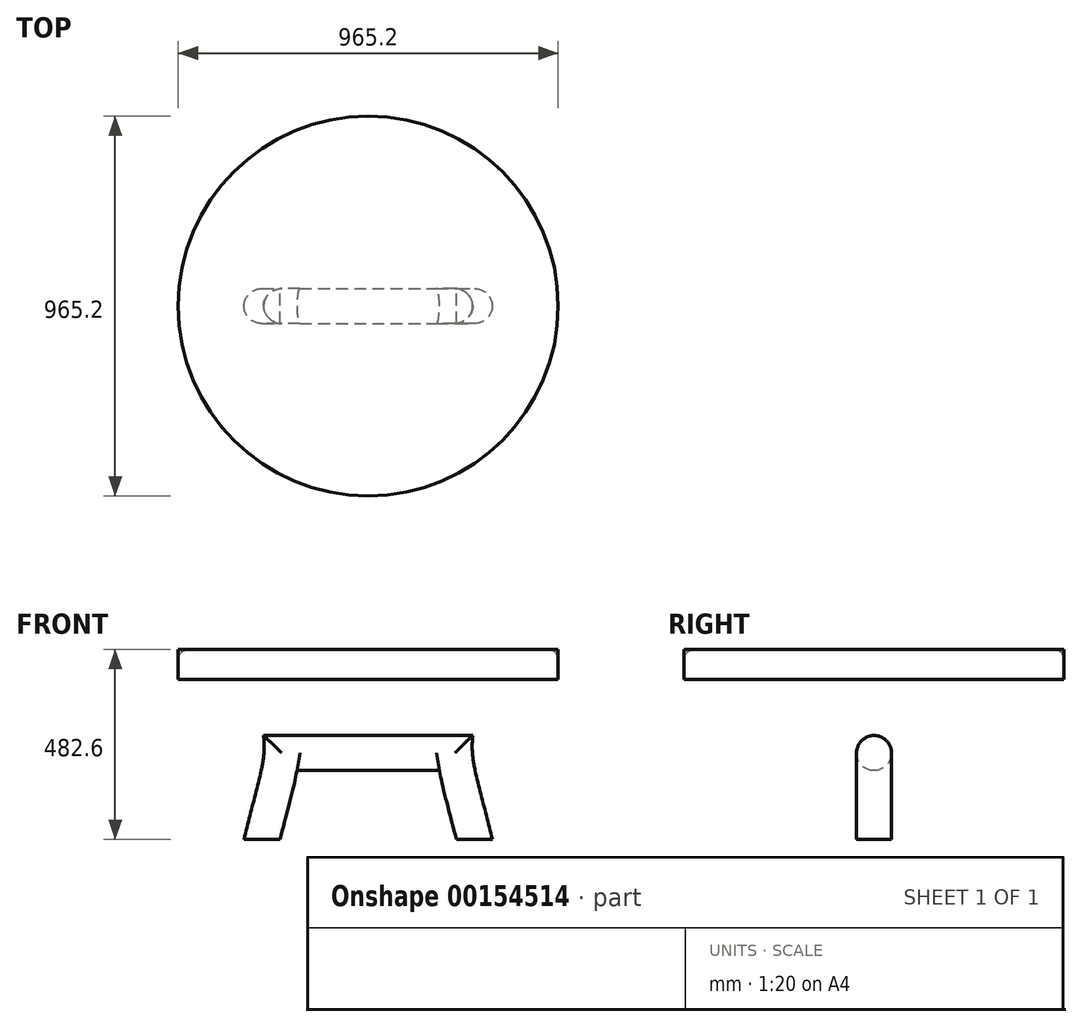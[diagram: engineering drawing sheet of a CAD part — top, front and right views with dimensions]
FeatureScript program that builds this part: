
annotation { "Feature Type Name" : "Feature", "Feature Type Description" : "" }
export const myFeature = defineFeature(function(context is Context, id is Id, definition is map)
    precondition{}
    {
        {
            var Q0;
            Q0=qCreatedBy(makeId("Top.planeOp"),FACE);
            var sketch = newSketch(context, id + "F0", { "sketchPlane" : qUnion([Q0])});
            skCircle(sketch, "E0", {"center": v(0, 0) * mm, "radius": 482.6 * mm});
            skSolve(sketch);
        }
        {
            var Q0;
            Q0=makeQuery(id+"F0.imprint","IMPRINT",FACE,{"disambiguationData":[TD([[makeQuery(id+"F0.imprint","IMPRINT",EDGE,{"derivedFrom":sQuery(id+"F0.wireOp",EDGE,"E0")}),1.0]])]});
            extrude(context, id + "F1", {"entities" : qUnion([Q0]), "oppositeDirection" : true, "depth" : 76.2 * mm});
        }
        {
            var Q0;
            Q0=qCreatedBy(makeId("Front.planeOp"),FACE);
            var sketch = newSketch(context, id + "F2", { "sketchPlane" : qUnion([Q0])});
            skFitSpline(sketch, "E1", {"points": [v(-350.08, -37.61) * mm, v(-265.93, -218.8) * mm, v(-315.3, -482.6) * mm], "startDerivative": vector(306.3, -378.15) * mm, "endDerivative": vector(-196.23, -818.74) * mm});
            skLineSegment(sketch, "E2", {"start": v(-315.3, -482.6) * mm, "end": v(-223.82, -482.6) * mm});
            skFitSpline(sketch, "E3.0", {"points": [v(-281, 18.35) * mm, v(-273.37, 8.93) * mm, v(-258.87, -10.26) * mm, v(-239.44, -39.86) * mm, v(-222.35, -70.1) * mm, v(-207.68, -100.8) * mm, v(-195.49, -131.86) * mm, v(-187.5, -157.95) * mm, v(-182.5, -178.94) * mm, v(-180, -192.1) * mm, v(-178.36, -202.68) * mm, v(-177, -213.27) * mm, v(-175.82, -226.5) * mm, v(-175.23, -242.3) * mm, v(-175.47, -257.95) * mm, v(-176.47, -273.39) * mm, v(-178.13, -288.6) * mm, v(-180.37, -303.66) * mm, v(-183.1, -318.64) * mm, v(-186.24, -333.69) * mm, v(-190.93, -354.09) * mm, v(-197.62, -380.68) * mm, v(-206.85, -415.9) * mm, v(-217.23, -455.92) * mm, v(-224.87, -486.7) * mm, v(-228.85, -503.32) * mm]});
            skLineSegment(sketch, "E4", {"start": v(0, 0) * mm, "end": v(0, -373.88) * mm, "construction": true});
            skFitSpline(sketch, "E5.MirrorCS", {"points": [v(350.08, -37.61) * mm, v(265.93, -218.8) * mm, v(315.3, -482.6) * mm], "startDerivative": vector(-306.3, -378.15) * mm, "endDerivative": vector(196.23, -818.74) * mm});
            skFitSpline(sketch, "E6.0", {"points": [v(281, 18.35) * mm, v(273.37, 8.93) * mm, v(258.87, -10.26) * mm, v(239.44, -39.86) * mm, v(222.35, -70.1) * mm, v(207.68, -100.8) * mm, v(195.49, -131.86) * mm, v(187.5, -157.95) * mm, v(182.5, -178.94) * mm, v(180, -192.1) * mm, v(178.36, -202.68) * mm, v(177, -213.27) * mm, v(175.82, -226.5) * mm, v(175.23, -242.3) * mm, v(175.47, -257.95) * mm, v(176.47, -273.39) * mm, v(178.13, -288.6) * mm, v(180.37, -303.66) * mm, v(183.1, -318.64) * mm, v(186.24, -333.69) * mm, v(190.93, -354.09) * mm, v(197.62, -380.68) * mm, v(206.85, -415.9) * mm, v(217.23, -455.92) * mm, v(224.87, -486.7) * mm, v(228.85, -503.32) * mm]});
            skLineSegment(sketch, "E7", {"start": v(-350.08, -37.61) * mm, "end": v(-241.28, -37.61) * mm});
            skLineSegment(sketch, "E8", {"start": v(350.08, -37.61) * mm, "end": v(241.28, -37.61) * mm});
            skLineSegment(sketch, "E9", {"start": v(265.93, -218.8) * mm, "end": v(-265.93, -218.8) * mm});
            skLineSegment(sketch, "E10", {"start": v(271.65, -307.7) * mm, "end": v(-271.65, -307.7) * mm});
            skLineSegment(sketch, "E11", {"start": v(223.82, -482.6) * mm, "end": v(315.3, -482.6) * mm});
            skSolve(sketch);
        }
        {
            var Q0;
            {var subQ0=sQuery(id+"F2.wireOp",EDGE,"E7");var subQ1=sQuery(id+"F2.wireOp",EDGE,"E1");var subQ2=makeQuery(id+"F2.imprint","INTERSECT",VERTEX,{"derivedFrom":[subQ1,subQ0]});Q0=makeQuery(id+"F2.imprint","IMPRINT",FACE,{"disambiguationData":[TD([[makeQuery(id+"F2.imprint","IMPRINT",EDGE,{"disambiguationData":[TD([[subQ2,-1.0]])],"derivedFrom":subQ1}),1.0]])]});}
            var Q1;
            {var subQ0=sQuery(id+"F2.wireOp",EDGE,"E9");var subQ1=sQuery(id+"F2.wireOp",EDGE,"E1");var subQ2=makeQuery(id+"F2.imprint","INTERSECT",VERTEX,{"derivedFrom":[subQ1,subQ0]});Q1=makeQuery(id+"F2.imprint","IMPRINT",FACE,{"disambiguationData":[TD([[makeQuery(id+"F2.imprint","IMPRINT",EDGE,{"disambiguationData":[TD([[subQ2,-1.0]])],"derivedFrom":subQ1}),1.0]])]});}
            var Q2;
            {var subQ0=sQuery(id+"F2.wireOp",EDGE,"E10");var subQ1=sQuery(id+"F2.wireOp",EDGE,"E3.0");var subQ2=makeQuery(id+"F2.imprint","INTERSECT",VERTEX,{"derivedFrom":[subQ1,subQ0]});Q2=makeQuery(id+"F2.imprint","IMPRINT",FACE,{"disambiguationData":[TD([[makeQuery(id+"F2.imprint","IMPRINT",EDGE,{"disambiguationData":[TD([[subQ2,1.0]])],"derivedFrom":subQ1}),1.0]])]});}
            var Q3;
            {var subQ0=sQuery(id+"F2.wireOp",EDGE,"E8");var subQ1=sQuery(id+"F2.wireOp",EDGE,"E5.MirrorCS");var subQ2=makeQuery(id+"F2.imprint","INTERSECT",VERTEX,{"derivedFrom":[subQ1,subQ0]});Q3=makeQuery(id+"F2.imprint","IMPRINT",FACE,{"disambiguationData":[TD([[makeQuery(id+"F2.imprint","IMPRINT",EDGE,{"disambiguationData":[TD([[subQ2,-1.0]])],"derivedFrom":subQ1}),-1.0]])]});}
            var Q4;
            {var subQ0=sQuery(id+"F2.wireOp",EDGE,"E9");var subQ1=sQuery(id+"F2.wireOp",EDGE,"E5.MirrorCS");var subQ2=makeQuery(id+"F2.imprint","INTERSECT",VERTEX,{"derivedFrom":[subQ1,subQ0]});Q4=makeQuery(id+"F2.imprint","IMPRINT",FACE,{"disambiguationData":[TD([[makeQuery(id+"F2.imprint","IMPRINT",EDGE,{"disambiguationData":[TD([[subQ2,-1.0]])],"derivedFrom":subQ1}),-1.0]])]});}
            var Q5;
            {var subQ0=sQuery(id+"F2.wireOp",EDGE,"E2");Q5=makeQuery(id+"F2.imprint","IMPRINT",FACE,{"disambiguationData":[TD([[makeQuery(id+"F2.imprint","IMPRINT",EDGE,{"derivedFrom":subQ0}),1.0]])]});}
            var Q6;
            {var subQ0=sQuery(id+"F2.wireOp",EDGE,"E11");var subQ1=sQuery(id+"F2.wireOp",EDGE,"E5.MirrorCS");var subQ2=makeQuery(id+"F2.imprint","INTERSECT",VERTEX,{"derivedFrom":[subQ1,subQ0]});Q6=makeQuery(id+"F2.imprint","IMPRINT",FACE,{"disambiguationData":[TD([[makeQuery(id+"F2.imprint","IMPRINT",EDGE,{"disambiguationData":[TD([[subQ2,1.0]])],"derivedFrom":subQ1}),-1.0]])]});}
            extrude(context, id + "F3", {"entities" : qUnion([Q0, Q1, Q2, Q3, Q4, Q5, Q6]), "operationType" : NewBodyOperationType.ADD, "depth" : 88.9 * mm, "symmetric" : true});
        }
        {
            var Q0;
            Q0=makeQuery(id+"F1.opExtrude","SWEPT_BODY",BODY,{"disambiguationData":[OSD([sQuery(id+"F0.wireOp",EDGE,"E0")])]});
            var Q1;
            Q1=makeQuery(id+"F1.opExtrude","CAP_EDGE",EDGE,{"disambiguationData":[OSD([sQuery(id+"F0.wireOp",EDGE,"E0")])],"isStart":true});
            circularPattern(context, id + "F4", {"operationType" : NewBodyOperationType.ADD, "entities" : qUnion([Q0]), "axis" : qUnion([Q1]), "angle" : 90 * degree, "instanceCount" : 2});
        }
        {
            var Q0;
            Q0=makeQuery(id+"F4.opPattern","COPY",EDGE,{"derivedFrom":makeQuery(id+"F3.opExtrude","CAP_EDGE",EDGE,{"disambiguationData":[OSD([sQuery(id+"F2.wireOp",EDGE,"E1")])],"isStart":false}),"instanceName":"1"});
            var Q1;
            Q1=makeQuery(id+"F4.opPattern","COPY",EDGE,{"derivedFrom":makeQuery(id+"F3.opExtrude","CAP_EDGE",EDGE,{"disambiguationData":[OSD([sQuery(id+"F2.wireOp",EDGE,"E1")])],"isStart":true}),"instanceName":"1"});
            var Q2;
            Q2=makeQuery(id+"F3.opExtrude","CAP_EDGE",EDGE,{"disambiguationData":[OSD([sQuery(id+"F2.wireOp",EDGE,"E5.MirrorCS")])],"isStart":false});
            var Q3;
            Q3=makeQuery(id+"F3.opExtrude","CAP_EDGE",EDGE,{"disambiguationData":[OSD([sQuery(id+"F2.wireOp",EDGE,"E5.MirrorCS")])],"isStart":true});
            var Q4;
            Q4=makeQuery(id+"F3.opExtrude","CAP_EDGE",EDGE,{"disambiguationData":[OSD([sQuery(id+"F2.wireOp",EDGE,"E1")])],"isStart":false});
            var Q5;
            Q5=makeQuery(id+"F3.opExtrude","CAP_EDGE",EDGE,{"disambiguationData":[OSD([sQuery(id+"F2.wireOp",EDGE,"E1")])],"isStart":true});
            var Q6;
            Q6=makeQuery(id+"F4.opPattern","COPY",EDGE,{"derivedFrom":makeQuery(id+"F3.opExtrude","CAP_EDGE",EDGE,{"disambiguationData":[OSD([sQuery(id+"F2.wireOp",EDGE,"E5.MirrorCS")])],"isStart":true}),"instanceName":"1"});
            var Q7;
            Q7=makeQuery(id+"F4.opPattern","COPY",EDGE,{"derivedFrom":makeQuery(id+"F3.opExtrude","CAP_EDGE",EDGE,{"disambiguationData":[OSD([sQuery(id+"F2.wireOp",EDGE,"E5.MirrorCS")])],"isStart":false}),"instanceName":"1"});
            var Q8;
            {var subQ0=makeQuery(id+"F3.opExtrude","CAP_FACE",FACE,{"disambiguationData":[OSD([sQuery(id+"F2.wireOp",EDGE,"E1"),sQuery(id+"F2.wireOp",EDGE,"E2"),sQuery(id+"F2.wireOp",EDGE,"E3.0"),sQuery(id+"F2.wireOp",EDGE,"E5.MirrorCS"),sQuery(id+"F2.wireOp",EDGE,"E6.0"),sQuery(id+"F2.wireOp",EDGE,"E7"),sQuery(id+"F2.wireOp",EDGE,"E8"),sQuery(id+"F2.wireOp",EDGE,"E9"),sQuery(id+"F2.wireOp",EDGE,"E10"),sQuery(id+"F2.wireOp",EDGE,"E11")])],"isStart":false});Q8=makeQuery(id+"F4.boolean.opBoolean","INTERSECT",EDGE,{"derivedFrom":[subQ0,makeQuery(id+"F4.opPattern","COPY",FACE,{"derivedFrom":subQ0,"instanceName":"1"})]});}
            var Q9;
            {var subQ0=sQuery(id+"F2.wireOp",EDGE,"E11");var subQ1=sQuery(id+"F2.wireOp",EDGE,"E10");var subQ2=sQuery(id+"F2.wireOp",EDGE,"E9");var subQ3=sQuery(id+"F2.wireOp",EDGE,"E8");var subQ4=sQuery(id+"F2.wireOp",EDGE,"E7");var subQ5=sQuery(id+"F2.wireOp",EDGE,"E6.0");var subQ6=sQuery(id+"F2.wireOp",EDGE,"E5.MirrorCS");var subQ7=sQuery(id+"F2.wireOp",EDGE,"E3.0");var subQ8=sQuery(id+"F2.wireOp",EDGE,"E2");var subQ9=sQuery(id+"F2.wireOp",EDGE,"E1");Q9=makeQuery(id+"F4.boolean.opBoolean","INTERSECT",EDGE,{"derivedFrom":[makeQuery(id+"F3.opExtrude","CAP_FACE",FACE,{"disambiguationData":[OSD([subQ9,subQ8,subQ7,subQ6,subQ5,subQ4,subQ3,subQ2,subQ1,subQ0])],"isStart":false}),makeQuery(id+"F4.opPattern","COPY",FACE,{"derivedFrom":makeQuery(id+"F3.opExtrude","CAP_FACE",FACE,{"disambiguationData":[OSD([subQ9,subQ8,subQ7,subQ6,subQ5,subQ4,subQ3,subQ2,subQ1,subQ0])],"isStart":true}),"instanceName":"1"})]});}
            var Q10;
            {var subQ0=makeQuery(id+"F3.opExtrude","CAP_FACE",FACE,{"disambiguationData":[OSD([sQuery(id+"F2.wireOp",EDGE,"E1"),sQuery(id+"F2.wireOp",EDGE,"E2"),sQuery(id+"F2.wireOp",EDGE,"E3.0"),sQuery(id+"F2.wireOp",EDGE,"E5.MirrorCS"),sQuery(id+"F2.wireOp",EDGE,"E6.0"),sQuery(id+"F2.wireOp",EDGE,"E7"),sQuery(id+"F2.wireOp",EDGE,"E8"),sQuery(id+"F2.wireOp",EDGE,"E9"),sQuery(id+"F2.wireOp",EDGE,"E10"),sQuery(id+"F2.wireOp",EDGE,"E11")])],"isStart":true});Q10=makeQuery(id+"F4.boolean.opBoolean","INTERSECT",EDGE,{"derivedFrom":[subQ0,makeQuery(id+"F4.opPattern","COPY",FACE,{"derivedFrom":subQ0,"instanceName":"1"})]});}
            var Q11;
            {var subQ0=sQuery(id+"F2.wireOp",EDGE,"E11");var subQ1=sQuery(id+"F2.wireOp",EDGE,"E10");var subQ2=sQuery(id+"F2.wireOp",EDGE,"E9");var subQ3=sQuery(id+"F2.wireOp",EDGE,"E8");var subQ4=sQuery(id+"F2.wireOp",EDGE,"E7");var subQ5=sQuery(id+"F2.wireOp",EDGE,"E6.0");var subQ6=sQuery(id+"F2.wireOp",EDGE,"E5.MirrorCS");var subQ7=sQuery(id+"F2.wireOp",EDGE,"E3.0");var subQ8=sQuery(id+"F2.wireOp",EDGE,"E2");var subQ9=sQuery(id+"F2.wireOp",EDGE,"E1");Q11=makeQuery(id+"F4.boolean.opBoolean","INTERSECT",EDGE,{"derivedFrom":[makeQuery(id+"F3.opExtrude","CAP_FACE",FACE,{"disambiguationData":[OSD([subQ9,subQ8,subQ7,subQ6,subQ5,subQ4,subQ3,subQ2,subQ1,subQ0])],"isStart":true}),makeQuery(id+"F4.opPattern","COPY",FACE,{"derivedFrom":makeQuery(id+"F3.opExtrude","CAP_FACE",FACE,{"disambiguationData":[OSD([subQ9,subQ8,subQ7,subQ6,subQ5,subQ4,subQ3,subQ2,subQ1,subQ0])],"isStart":false}),"instanceName":"1"})]});}
            var Q12;
            {var subQ0=sQuery(id+"F2.wireOp",EDGE,"E9");var subQ2=sQuery(id+"F2.wireOp",EDGE,"E8");var subQ3=sQuery(id+"F2.wireOp",EDGE,"E6.0");Q12=makeQuery(id+"F4.boolean.opBoolean","SPLIT",EDGE,{"disambiguationData":[TD([makeQuery(id+"F3.opExtrude","SWEPT_FACE",FACE,{"disambiguationData":[OSD([subQ3]),TDD([makeQuery(id+"F2.imprint","IMPRINT",EDGE,{"disambiguationData":[TD([[makeQuery(id+"F2.imprint","INTERSECT",VERTEX,{"derivedFrom":[subQ3,subQ2]}),-1.0]])],"derivedFrom":subQ3})])]})])],"derivedFrom":makeQuery(id+"F3.opExtrude","CAP_EDGE",EDGE,{"disambiguationData":[OSD([subQ0])],"isStart":true})});}
            var Q13;
            {var subQ0=sQuery(id+"F2.wireOp",EDGE,"E9");var subQ2=sQuery(id+"F2.wireOp",EDGE,"E8");var subQ3=sQuery(id+"F2.wireOp",EDGE,"E6.0");Q13=makeQuery(id+"F4.boolean.opBoolean","SPLIT",EDGE,{"disambiguationData":[TD([makeQuery(id+"F3.opExtrude","SWEPT_FACE",FACE,{"disambiguationData":[OSD([subQ3]),TDD([makeQuery(id+"F2.imprint","IMPRINT",EDGE,{"disambiguationData":[TD([[makeQuery(id+"F2.imprint","INTERSECT",VERTEX,{"derivedFrom":[subQ3,subQ2]}),-1.0]])],"derivedFrom":subQ3})])]})])],"derivedFrom":makeQuery(id+"F3.opExtrude","CAP_EDGE",EDGE,{"disambiguationData":[OSD([subQ0])],"isStart":false})});}
            var Q14;
            {var subQ0=sQuery(id+"F2.wireOp",EDGE,"E9");var subQ2=sQuery(id+"F2.wireOp",EDGE,"E7");var subQ3=sQuery(id+"F2.wireOp",EDGE,"E3.0");Q14=makeQuery(id+"F4.boolean.opBoolean","SPLIT",EDGE,{"disambiguationData":[TD([makeQuery(id+"F3.opExtrude","SWEPT_FACE",FACE,{"disambiguationData":[OSD([subQ3]),TDD([makeQuery(id+"F2.imprint","IMPRINT",EDGE,{"disambiguationData":[TD([[makeQuery(id+"F2.imprint","INTERSECT",VERTEX,{"derivedFrom":[subQ3,subQ2]}),-1.0]])],"derivedFrom":subQ3})])]})])],"derivedFrom":makeQuery(id+"F3.opExtrude","CAP_EDGE",EDGE,{"disambiguationData":[OSD([subQ0])],"isStart":true})});}
            var Q15;
            {var subQ2=sQuery(id+"F2.wireOp",EDGE,"E9");var subQ4=sQuery(id+"F2.wireOp",EDGE,"E7");var subQ7=sQuery(id+"F2.wireOp",EDGE,"E3.0");Q15=makeQuery(id+"F4.boolean.opBoolean","SPLIT",EDGE,{"disambiguationData":[TD([makeQuery(id+"F4.opPattern","COPY",FACE,{"derivedFrom":makeQuery(id+"F3.opExtrude","SWEPT_FACE",FACE,{"disambiguationData":[OSD([subQ7]),TDD([makeQuery(id+"F2.imprint","IMPRINT",EDGE,{"disambiguationData":[TD([[makeQuery(id+"F2.imprint","INTERSECT",VERTEX,{"derivedFrom":[subQ7,subQ4]}),-1.0]])],"derivedFrom":subQ7})])]}),"instanceName":"1"})])],"derivedFrom":makeQuery(id+"F4.opPattern","COPY",EDGE,{"derivedFrom":makeQuery(id+"F3.opExtrude","CAP_EDGE",EDGE,{"disambiguationData":[OSD([subQ2])],"isStart":true}),"instanceName":"1"})});}
            var Q16;
            {var subQ0=sQuery(id+"F2.wireOp",EDGE,"E10");var subQ2=sQuery(id+"F2.wireOp",EDGE,"E11");var subQ3=sQuery(id+"F2.wireOp",EDGE,"E6.0");Q16=makeQuery(id+"F4.boolean.opBoolean","SPLIT",EDGE,{"disambiguationData":[TD([makeQuery(id+"F4.opPattern","COPY",FACE,{"derivedFrom":makeQuery(id+"F3.opExtrude","SWEPT_FACE",FACE,{"disambiguationData":[OSD([subQ3]),TDD([makeQuery(id+"F2.imprint","IMPRINT",EDGE,{"disambiguationData":[TD([[makeQuery(id+"F2.imprint","INTERSECT",VERTEX,{"derivedFrom":[subQ3,subQ2]}),1.0]])],"derivedFrom":subQ3})])]}),"instanceName":"1"})])],"derivedFrom":makeQuery(id+"F4.opPattern","COPY",EDGE,{"derivedFrom":makeQuery(id+"F3.opExtrude","CAP_EDGE",EDGE,{"disambiguationData":[OSD([subQ0])],"isStart":true}),"instanceName":"1"})});}
            var Q17;
            {var subQ0=sQuery(id+"F2.wireOp",EDGE,"E10");var subQ8=sQuery(id+"F2.wireOp",EDGE,"E3.0");var subQ9=sQuery(id+"F2.wireOp",EDGE,"E2");Q17=makeQuery(id+"F4.boolean.opBoolean","SPLIT",EDGE,{"disambiguationData":[TD([makeQuery(id+"F3.opExtrude","SWEPT_FACE",FACE,{"disambiguationData":[OSD([subQ8]),TDD([makeQuery(id+"F2.imprint","IMPRINT",EDGE,{"disambiguationData":[TD([[makeQuery(id+"F2.imprint","INTERSECT",VERTEX,{"derivedFrom":[subQ9,subQ8]}),1.0]])],"derivedFrom":subQ8})])]})])],"derivedFrom":makeQuery(id+"F3.opExtrude","CAP_EDGE",EDGE,{"disambiguationData":[OSD([subQ0])],"isStart":false})});}
            var Q18;
            {var subQ0=sQuery(id+"F2.wireOp",EDGE,"E10");var subQ2=sQuery(id+"F2.wireOp",EDGE,"E11");var subQ3=sQuery(id+"F2.wireOp",EDGE,"E6.0");Q18=makeQuery(id+"F4.boolean.opBoolean","SPLIT",EDGE,{"disambiguationData":[TD([makeQuery(id+"F3.opExtrude","SWEPT_FACE",FACE,{"disambiguationData":[OSD([subQ3]),TDD([makeQuery(id+"F2.imprint","IMPRINT",EDGE,{"disambiguationData":[TD([[makeQuery(id+"F2.imprint","INTERSECT",VERTEX,{"derivedFrom":[subQ3,subQ2]}),1.0]])],"derivedFrom":subQ3})])]})])],"derivedFrom":makeQuery(id+"F3.opExtrude","CAP_EDGE",EDGE,{"disambiguationData":[OSD([subQ0])],"isStart":false})});}
            var Q19;
            {var subQ0=sQuery(id+"F2.wireOp",EDGE,"E10");var subQ2=sQuery(id+"F2.wireOp",EDGE,"E11");var subQ3=sQuery(id+"F2.wireOp",EDGE,"E6.0");Q19=makeQuery(id+"F4.boolean.opBoolean","SPLIT",EDGE,{"disambiguationData":[TD([makeQuery(id+"F3.opExtrude","SWEPT_FACE",FACE,{"disambiguationData":[OSD([subQ3]),TDD([makeQuery(id+"F2.imprint","IMPRINT",EDGE,{"disambiguationData":[TD([[makeQuery(id+"F2.imprint","INTERSECT",VERTEX,{"derivedFrom":[subQ3,subQ2]}),1.0]])],"derivedFrom":subQ3})])]})])],"derivedFrom":makeQuery(id+"F3.opExtrude","CAP_EDGE",EDGE,{"disambiguationData":[OSD([subQ0])],"isStart":true})});}
            fillet(context, id + "F5", {"entities" : qUnion([Q0, Q1, Q2, Q3, Q4, Q5, Q6, Q7, Q8, Q9, Q10, Q11, Q12, Q13, Q14, Q15, Q16, Q17, Q18, Q19]), "radius" : 44.45 * mm, "tangentPropagation" : true, "allowEdgeOverflow" : false});
        }
        {
            var Q0;
            Q0=makeQuery(id+"F1.opExtrude","CAP_FACE",FACE,{"disambiguationData":[OSD([sQuery(id+"F0.wireOp",EDGE,"E0")])],"isStart":true});
            fillet(context, id + "F6", {"entities" : qUnion([Q0]), "radius" : 25.4 * mm, "tangentPropagation" : true, "allowEdgeOverflow" : false});
        }
    });
